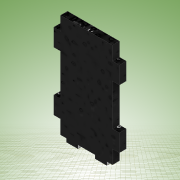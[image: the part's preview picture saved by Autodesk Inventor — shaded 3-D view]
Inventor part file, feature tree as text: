
AUTODESK INVENTOR PART (.ipt)
format: ipt  version: 2022 (Build 260153000, 153)  size: 163,328 bytes
history: native  units: mm
features: extrude x2, sketch x2, other x1
ambient origin geometry x8: Origin, YZ Plane, XZ Plane, XY Plane, X Axis, Y Axis, Z Axis, Center Point
bodies: Body1 (feature_tree)
feature tree (5):
  other  "Sólido1"
  extrude  "Extrusión1"  Depth=90.0mm
  extrude  "Extrusión2"  Depth=15.0mm
  sketch  "Boceto1"  dims[d0=45.0mm d1=90.0mm]
  sketch  "Boceto2"  dims[d2=6.0mm d3=15.0mm d4=12.0mm d5=6.0mm d6=0.0mm d7=10.0mm d8=5.0mm d9=3.0mm d10=0.0mm]
